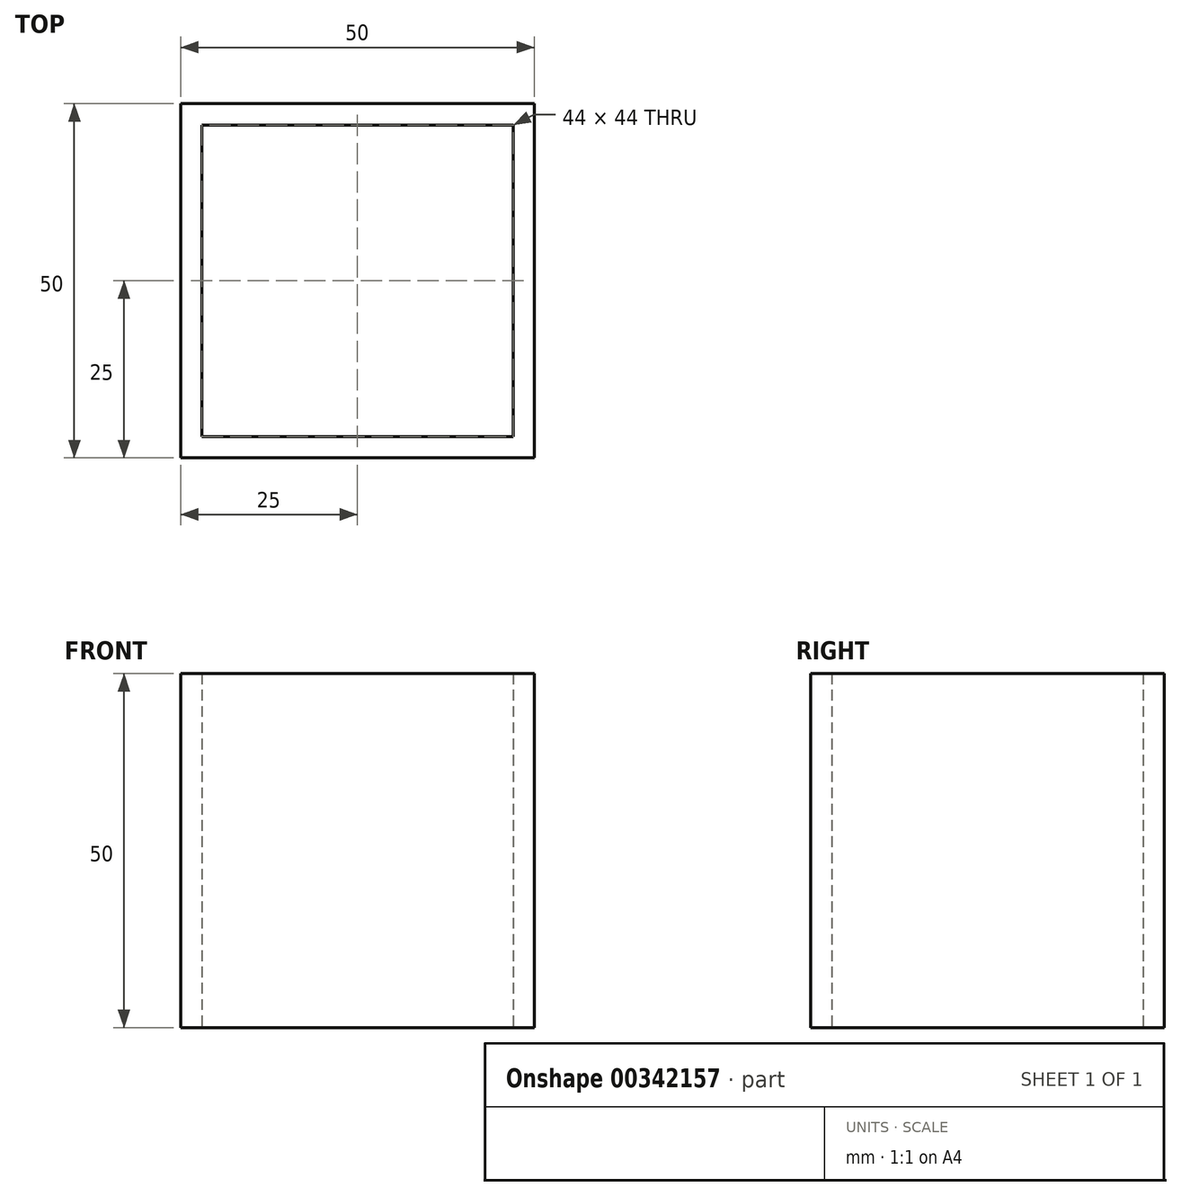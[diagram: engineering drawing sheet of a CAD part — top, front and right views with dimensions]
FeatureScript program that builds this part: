
annotation { "Feature Type Name" : "Feature", "Feature Type Description" : "" }
export const myFeature = defineFeature(function(context is Context, id is Id, definition is map)
    precondition{}
    {
        {
            var Q0;
            Q0=qCreatedBy(makeId("Top.planeOp"),FACE);
            var sketch = newSketch(context, id + "F0", { "sketchPlane" : qUnion([Q0])});
            skLineSegment(sketch, "E0.bottom", {"start": v(-25, 25) * mm, "end": v(25, 25) * mm});
            skLineSegment(sketch, "E0.top", {"start": v(-25, -25) * mm, "end": v(25, -25) * mm});
            skLineSegment(sketch, "E0.left", {"start": v(-25, 25) * mm, "end": v(-25, -25) * mm});
            skLineSegment(sketch, "E0.right", {"start": v(25, 25) * mm, "end": v(25, -25) * mm});
            skPoint(sketch, "E0.middle", {"position": v(0, 0) * mm});
            skLineSegment(sketch, "E1.bottom", {"start": v(-22, 22) * mm, "end": v(22, 22) * mm});
            skLineSegment(sketch, "E1.top", {"start": v(-22, -22) * mm, "end": v(22, -22) * mm});
            skLineSegment(sketch, "E1.left", {"start": v(-22, 22) * mm, "end": v(-22, -22) * mm});
            skLineSegment(sketch, "E1.right", {"start": v(22, 22) * mm, "end": v(22, -22) * mm});
            skSolve(sketch);
        }
        {
            var Q0;
            Q0=makeQuery(id+"F0.imprint","IMPRINT",FACE,{"disambiguationData":[TD([[makeQuery(id+"F0.imprint","IMPRINT",EDGE,{"derivedFrom":sQuery(id+"F0.wireOp",EDGE,"E0.bottom")}),-1.0]])]});
            extrude(context, id + "F1", {"entities" : qUnion([Q0]), "endBound" : BoundingType.SYMMETRIC, "depth" : 50 * mm});
        }
    });
